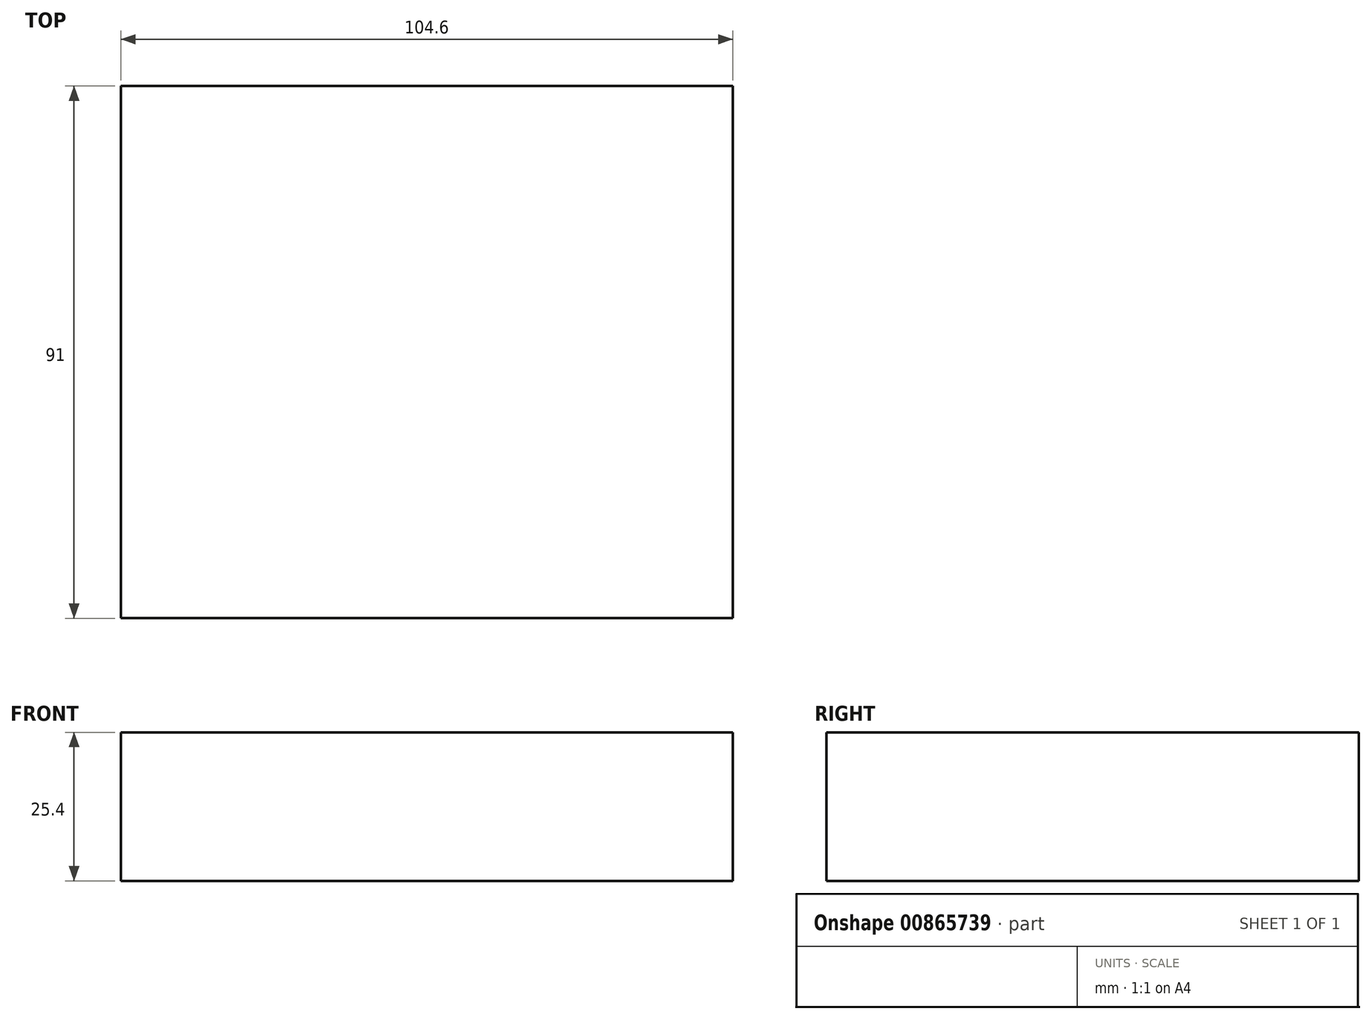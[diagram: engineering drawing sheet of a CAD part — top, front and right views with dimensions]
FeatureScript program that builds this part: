
annotation { "Feature Type Name" : "Feature", "Feature Type Description" : "" }
export const myFeature = defineFeature(function(context is Context, id is Id, definition is map)
    precondition{}
    {
        {
            var Q0;
            Q0=qCreatedBy(makeId("Top.planeOp"),FACE);
            var sketch = newSketch(context, id + "F0", { "sketchPlane" : qUnion([Q0])});
            skLineSegment(sketch, "E0.bottom", {"start": v(52.3, 45.5) * mm, "end": v(-52.3, 45.5) * mm});
            skLineSegment(sketch, "E0.top", {"start": v(52.3, -45.5) * mm, "end": v(-52.3, -45.5) * mm});
            skLineSegment(sketch, "E0.left", {"start": v(52.3, 45.5) * mm, "end": v(52.3, -45.5) * mm});
            skLineSegment(sketch, "E0.right", {"start": v(-52.3, 45.5) * mm, "end": v(-52.3, -45.5) * mm});
            skPoint(sketch, "E0.middle", {"position": v(0, 0) * mm});
            skSolve(sketch);
        }
        {
            var Q0;
            Q0 = qSketchRegion(id + "F0", true);
            var Q1;
            Q1=makeQuery(id+"F0.imprint","IMPRINT",FACE,{"disambiguationData":[TD([[makeQuery(id+"F0.imprint","IMPRINT",EDGE,{"derivedFrom":sQuery(id+"F0.wireOp",EDGE,"E0.bottom")}),1.0]])]});
            extrude(context, id + "F1", {"entities" : qUnion([Q0, Q1]), "depth" : 25.4 * mm, "offsetDistance" : 25.4 * mm});
        }
    });
